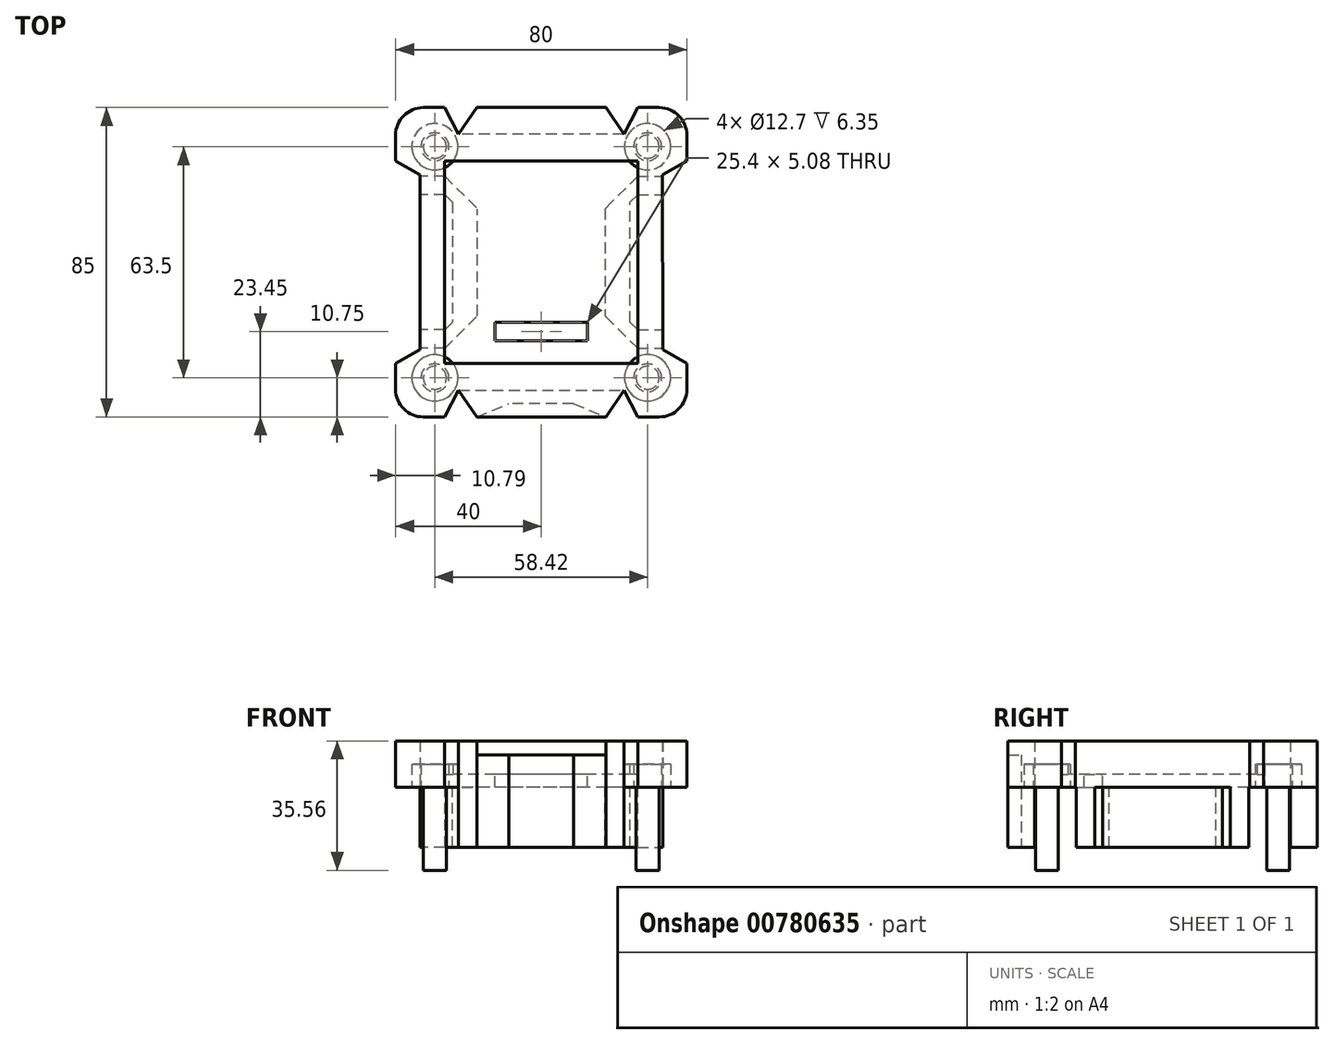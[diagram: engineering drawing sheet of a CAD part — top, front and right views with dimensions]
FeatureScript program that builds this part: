
annotation { "Feature Type Name" : "Feature", "Feature Type Description" : "" }
export const myFeature = defineFeature(function(context is Context, id is Id, definition is map)
    precondition{}
    {
        {
            var Q0;
            Q0=qCreatedBy(makeId("Top.planeOp"),FACE);
            var sketch = newSketch(context, id + "F0", { "sketchPlane" : qUnion([Q0])});
            skLineSegment(sketch, "E0.bottom", {"start": v(40, -42.5) * mm, "end": v(-40, -42.5) * mm});
            skLineSegment(sketch, "E0.top", {"start": v(40, 42.5) * mm, "end": v(-40, 42.5) * mm});
            skLineSegment(sketch, "E0.left", {"start": v(40, -42.5) * mm, "end": v(40, 42.5) * mm});
            skLineSegment(sketch, "E0.right", {"start": v(-40, -42.5) * mm, "end": v(-40, 42.5) * mm});
            skPoint(sketch, "E0.middle", {"position": v(0, 0) * mm});
            skSolve(sketch);
        }
        {
            var Q0;
            Q0=makeQuery(id+"F0.imprint","IMPRINT",FACE,{"disambiguationData":[TD([[makeQuery(id+"F0.imprint","IMPRINT",EDGE,{"derivedFrom":sQuery(id+"F0.wireOp",EDGE,"E0.bottom")}),-1.0]])]});
            extrude(context, id + "F1", {"entities" : qUnion([Q0]), "depth" : 25.4 * mm, "offsetDistance" : 25.4 * mm});
        }
        {
            var Q0;
            Q0=qCreatedBy(makeId("Front.planeOp"),FACE);
            var sketch = newSketch(context, id + "F2", { "sketchPlane" : qUnion([Q0])});
            skLineSegment(sketch, "E1.bottom", {"start": v(26.5, 3.57) * mm, "end": v(-26.5, 3.56) * mm});
            skLineSegment(sketch, "E1.top", {"start": v(26.5, 20.57) * mm, "end": v(-26.5, 20.56) * mm});
            skLineSegment(sketch, "E1.left", {"start": v(26.5, 3.57) * mm, "end": v(26.5, 20.57) * mm});
            skLineSegment(sketch, "E1.right", {"start": v(-26.5, 3.56) * mm, "end": v(-26.5, 20.57) * mm});
            skPoint(sketch, "E1.middle", {"position": v(0, 12.07) * mm});
            skSolve(sketch);
        }
        {
            var Q0;
            Q0=qSketchRegion(id+"F2",true);
            extrude(context, id + "F3", {"entities" : qUnion([Q0]), "operationType" : NewBodyOperationType.REMOVE, "oppositeDirection" : true, "depth" : 55.55 * mm, "offsetDistance" : 25.4 * mm, "symmetric" : true});
        }
        {
            var Q0;
            Q0=makeQuery(id+"F1.opExtrude","CAP_FACE",FACE,{"disambiguationData":[OSD([sQuery(id+"F0.wireOp",EDGE,"E0.bottom"),sQuery(id+"F0.wireOp",EDGE,"E0.top"),sQuery(id+"F0.wireOp",EDGE,"E0.left"),sQuery(id+"F0.wireOp",EDGE,"E0.right")])],"isStart":false});
            var sketch = newSketch(context, id + "F4", { "sketchPlane" : qUnion([Q0])});
            skLineSegment(sketch, "E2.bottom", {"start": v(40, -42.5) * mm, "end": v(-40, -42.5) * mm});
            skLineSegment(sketch, "E2.top", {"start": v(40, 42.5) * mm, "end": v(-40, 42.5) * mm});
            skLineSegment(sketch, "E2.left", {"start": v(40, -42.5) * mm, "end": v(40, 42.5) * mm});
            skLineSegment(sketch, "E2.right", {"start": v(-40, -42.5) * mm, "end": v(-40, 42.5) * mm});
            skPoint(sketch, "E2.middle", {"position": v(0, 0) * mm});
            skSolve(sketch);
        }
        {
            var Q0;
            Q0=qSketchRegion(id+"F4",true);
            extrude(context, id + "F5", {"entities" : qUnion([Q0]), "operationType" : NewBodyOperationType.REMOVE, "oppositeDirection" : true, "depth" : 12.7 * mm, "offsetDistance" : 25.4 * mm});
        }
        {
            var Q0;
            Q0=makeQuery(id+"F1.opExtrude","CAP_FACE",FACE,{"disambiguationData":[OSD([sQuery(id+"F0.wireOp",EDGE,"E0.bottom"),sQuery(id+"F0.wireOp",EDGE,"E0.top"),sQuery(id+"F0.wireOp",EDGE,"E0.left"),sQuery(id+"F0.wireOp",EDGE,"E0.right")])],"isStart":true});
            var sketch = newSketch(context, id + "F6", { "sketchPlane" : qUnion([Q0])});
            skCircle(sketch, "E3", {"center": v(-29.21, 31.75) * mm, "radius": 3.16 * mm});
            skCircle(sketch, "E4", {"center": v(29.21, 31.75) * mm, "radius": 3.16 * mm});
            skCircle(sketch, "E5", {"center": v(29.21, -31.75) * mm, "radius": 3.16 * mm});
            skCircle(sketch, "E6", {"center": v(-29.21, -31.75) * mm, "radius": 3.16 * mm});
            skSolve(sketch);
        }
        {
            var Q0;
            Q0 = qSketchRegion(id + "F6", true);
            extrude(context, id + "F7", {"entities" : qUnion([Q0]), "operationType" : NewBodyOperationType.ADD, "depth" : 22.86 * mm, "offsetDistance" : 25.4 * mm});
        }
        {
            var Q0;
            Q0=makeQuery(id+"F3.boolean.opBoolean","COPY",FACE,{"derivedFrom":makeQuery(id+"F3.opExtrude","SWEPT_FACE",FACE,{"disambiguationData":[OSD([sQuery(id+"F2.wireOp",EDGE,"E1.bottom")])]})});
            var sketch = newSketch(context, id + "F8", { "sketchPlane" : qUnion([Q0])});
            skLineSegment(sketch, "E7.bottom", {"start": v(12.7, -21.59) * mm, "end": v(-12.7, -21.59) * mm});
            skLineSegment(sketch, "E7.top", {"start": v(12.7, -16.51) * mm, "end": v(-12.7, -16.51) * mm});
            skLineSegment(sketch, "E7.left", {"start": v(12.7, -21.59) * mm, "end": v(12.7, -16.51) * mm});
            skLineSegment(sketch, "E7.right", {"start": v(-12.7, -21.59) * mm, "end": v(-12.7, -16.51) * mm});
            skPoint(sketch, "E7.middle", {"position": v(0, -19.05) * mm});
            skSolve(sketch);
        }
        {
            var Q0;
            Q0 = qSketchRegion(id + "F8", true);
            extrude(context, id + "F9", {"entities" : qUnion([Q0]), "operationType" : NewBodyOperationType.REMOVE, "oppositeDirection" : true, "depth" : 25.4 * mm, "offsetDistance" : 25.4 * mm});
        }
        {
            var Q0;
            Q0=makeQuery(id+"F1.opExtrude","SWEPT_EDGE",EDGE,{"disambiguationData":[OSD([sQuery(id+"F0.wireOp",EDGE,"E0.bottom"),sQuery(id+"F0.wireOp",EDGE,"E0.right")])]});
            fillet(context, id + "F10", {"entities" : qUnion([Q0]), "radius" : 7.62 * mm, "tangentPropagation" : true, "allowEdgeOverflow" : false});
        }
        {
            var Q0;
            Q0=makeQuery(id+"F1.opExtrude","SWEPT_EDGE",EDGE,{"disambiguationData":[OSD([sQuery(id+"F0.wireOp",EDGE,"E0.top"),sQuery(id+"F0.wireOp",EDGE,"E0.right")])]});
            fillet(context, id + "F11", {"entities" : qUnion([Q0]), "radius" : 7.62 * mm, "tangentPropagation" : true, "allowEdgeOverflow" : false});
        }
        {
            var Q0;
            Q0=makeQuery(id+"F1.opExtrude","SWEPT_EDGE",EDGE,{"disambiguationData":[OSD([sQuery(id+"F0.wireOp",EDGE,"E0.top"),sQuery(id+"F0.wireOp",EDGE,"E0.left")])]});
            fillet(context, id + "F12", {"entities" : qUnion([Q0]), "radius" : 7.62 * mm, "tangentPropagation" : true, "allowEdgeOverflow" : false});
        }
        {
            var Q0;
            Q0=makeQuery(id+"F1.opExtrude","SWEPT_EDGE",EDGE,{"disambiguationData":[OSD([sQuery(id+"F0.wireOp",EDGE,"E0.bottom"),sQuery(id+"F0.wireOp",EDGE,"E0.left")])]});
            fillet(context, id + "F13", {"entities" : qUnion([Q0]), "radius" : 7.62 * mm, "tangentPropagation" : true, "allowEdgeOverflow" : false});
        }
        {
            var Q0;
            Q0=makeQuery(id+"F1.opExtrude","CAP_FACE",FACE,{"disambiguationData":[OSD([sQuery(id+"F0.wireOp",EDGE,"E0.bottom"),sQuery(id+"F0.wireOp",EDGE,"E0.top"),sQuery(id+"F0.wireOp",EDGE,"E0.left"),sQuery(id+"F0.wireOp",EDGE,"E0.right")])],"isStart":true});
            var sketch = newSketch(context, id + "F14", { "sketchPlane" : qUnion([Q0])});
            skLineSegment(sketch, "E8", {"start": v(-26.48, 23.65) * mm, "end": v(-19.3, 16.47) * mm});
            skLineSegment(sketch, "E9", {"start": v(-26.48, -23.65) * mm, "end": v(-19.3, -16.47) * mm});
            skLineSegment(sketch, "E10", {"start": v(-24.38, -8.23) * mm, "end": v(-24.38, -16.47) * mm});
            skLineSegment(sketch, "E11", {"start": v(-24.38, -16.47) * mm, "end": v(-26.48, -18.57) * mm});
            skLineSegment(sketch, "E12", {"start": v(-24.38, -8.23) * mm, "end": v(-24.38, 0) * mm});
            skLineSegment(sketch, "E13", {"start": v(-24.38, 8.23) * mm, "end": v(-24.38, 0) * mm});
            skLineSegment(sketch, "E14", {"start": v(-24.38, 8.23) * mm, "end": v(-24.38, 16.47) * mm});
            skLineSegment(sketch, "E15", {"start": v(-24.38, 16.47) * mm, "end": v(-26.48, 18.57) * mm});
            skLineSegment(sketch, "E16", {"start": v(-26.48, 18.57) * mm, "end": v(-34.1, 18.57) * mm});
            skLineSegment(sketch, "E17", {"start": v(-26.48, 23.65) * mm, "end": v(-34.1, 23.65) * mm});
            skLineSegment(sketch, "E18", {"start": v(-34.1, 23.65) * mm, "end": v(-34.1, 18.57) * mm});
            skLineSegment(sketch, "E19", {"start": v(-26.48, -18.57) * mm, "end": v(-34.1, -18.57) * mm});
            skLineSegment(sketch, "E20", {"start": v(-26.48, -23.65) * mm, "end": v(-34.1, -23.65) * mm});
            skLineSegment(sketch, "E21", {"start": v(-34.1, -23.65) * mm, "end": v(-34.1, -18.57) * mm});
            skLineSegment(sketch, "E22", {"start": v(26.48, -23.65) * mm, "end": v(19.3, -16.47) * mm});
            skLineSegment(sketch, "E23", {"start": v(26.48, 23.65) * mm, "end": v(19.3, 16.47) * mm});
            skLineSegment(sketch, "E24", {"start": v(24.38, 8.23) * mm, "end": v(24.38, 16.47) * mm});
            skLineSegment(sketch, "E25", {"start": v(24.38, 16.47) * mm, "end": v(26.48, 18.57) * mm});
            skLineSegment(sketch, "E26", {"start": v(24.38, 8.23) * mm, "end": v(24.38, 0) * mm});
            skLineSegment(sketch, "E27", {"start": v(24.38, -8.23) * mm, "end": v(24.38, 0) * mm});
            skLineSegment(sketch, "E28", {"start": v(24.38, -8.23) * mm, "end": v(24.38, -16.47) * mm});
            skLineSegment(sketch, "E29", {"start": v(24.38, -16.47) * mm, "end": v(26.48, -18.57) * mm});
            skLineSegment(sketch, "E30", {"start": v(26.48, -18.57) * mm, "end": v(34.1, -18.57) * mm});
            skLineSegment(sketch, "E31", {"start": v(26.48, -23.65) * mm, "end": v(34.1, -23.65) * mm});
            skLineSegment(sketch, "E32", {"start": v(34.1, -23.65) * mm, "end": v(34.1, -18.57) * mm});
            skLineSegment(sketch, "E33", {"start": v(26.48, 18.57) * mm, "end": v(34.1, 18.57) * mm});
            skLineSegment(sketch, "E34", {"start": v(34.1, 18.57) * mm, "end": v(34.1, 23.65) * mm});
            skLineSegment(sketch, "E35", {"start": v(26.48, 23.65) * mm, "end": v(34.1, 23.65) * mm});
            skLineSegment(sketch, "E36", {"start": v(-17.5, 14.67) * mm, "end": v(-17.5, 0) * mm});
            skLineSegment(sketch, "E37", {"start": v(-19.3, 16.47) * mm, "end": v(-17.5, 14.67) * mm});
            skLineSegment(sketch, "E38", {"start": v(-17.5, 0) * mm, "end": v(-17.5, -14.67) * mm});
            skLineSegment(sketch, "E39", {"start": v(-19.3, -16.47) * mm, "end": v(-17.5, -14.67) * mm});
            skLineSegment(sketch, "E40", {"start": v(17.5, 0) * mm, "end": v(17.5, 14.67) * mm});
            skLineSegment(sketch, "E41", {"start": v(17.5, 14.67) * mm, "end": v(19.3, 16.47) * mm});
            skLineSegment(sketch, "E42", {"start": v(17.5, 0) * mm, "end": v(17.5, -14.67) * mm});
            skLineSegment(sketch, "E43", {"start": v(19.3, -16.47) * mm, "end": v(17.5, -14.67) * mm});
            skSolve(sketch);
        }
        {
            var Q0;
            Q0 = qSketchRegion(id + "F14", true);
            extrude(context, id + "F15", {"entities" : qUnion([Q0]), "operationType" : NewBodyOperationType.ADD, "depth" : 16.5 * mm, "offsetDistance" : 25.4 * mm});
        }
        {
            var Q0;
            Q0=makeQuery(id+"F1.opExtrude","CAP_FACE",FACE,{"disambiguationData":[OSD([sQuery(id+"F0.wireOp",EDGE,"E0.bottom"),sQuery(id+"F0.wireOp",EDGE,"E0.top"),sQuery(id+"F0.wireOp",EDGE,"E0.left"),sQuery(id+"F0.wireOp",EDGE,"E0.right")])],"isStart":true});
            var sketch = newSketch(context, id + "F16", { "sketchPlane" : qUnion([Q0])});
            skLineSegment(sketch, "E44.bottom", {"start": v(-17.5, -25.4) * mm, "end": v(17.5, -25.4) * mm});
            skLineSegment(sketch, "E44.top", {"start": v(-17.5, 25.4) * mm, "end": v(17.5, 25.4) * mm});
            skLineSegment(sketch, "E44.left", {"start": v(-17.5, -25.4) * mm, "end": v(-17.5, 25.4) * mm});
            skLineSegment(sketch, "E44.right", {"start": v(17.5, -25.4) * mm, "end": v(17.5, 25.4) * mm});
            skPoint(sketch, "E44.middle", {"position": v(0, 0) * mm});
            skSolve(sketch);
        }
        {
            var Q0;
            Q0 = qSketchRegion(id + "F16", true);
            extrude(context, id + "F17", {"entities" : qUnion([Q0]), "operationType" : NewBodyOperationType.REMOVE, "depth" : 25.4 * mm, "offsetDistance" : 25.4 * mm});
        }
        {
            var Q0;
            Q0=makeQuery(id+"F3.boolean.opBoolean","COPY",FACE,{"derivedFrom":makeQuery(id+"F3.opExtrude","SWEPT_FACE",FACE,{"disambiguationData":[OSD([sQuery(id+"F2.wireOp",EDGE,"E1.bottom")])]})});
            var sketch = newSketch(context, id + "F18", { "sketchPlane" : qUnion([Q0])});
            skLineSegment(sketch, "E45", {"start": v(26.5, -42.5) * mm, "end": v(22.69, -35.14) * mm});
            skLineSegment(sketch, "E46", {"start": v(-22.69, -35.14) * mm, "end": v(-26.5, -42.5) * mm});
            skLineSegment(sketch, "E47", {"start": v(40, -27.77) * mm, "end": v(33.33, -24) * mm});
            skLineSegment(sketch, "E48", {"start": v(33.25, 23.96) * mm, "end": v(33.33, -24) * mm});
            skLineSegment(sketch, "E49", {"start": v(40, 27.77) * mm, "end": v(33.25, 23.96) * mm});
            skLineSegment(sketch, "E50", {"start": v(-22.69, 35.14) * mm, "end": v(22.69, 35.14) * mm});
            skLineSegment(sketch, "E51", {"start": v(26.5, 42.5) * mm, "end": v(22.69, 35.14) * mm});
            skLineSegment(sketch, "E52", {"start": v(-26.5, 42.5) * mm, "end": v(-22.69, 35.14) * mm});
            skLineSegment(sketch, "E53", {"start": v(-33.25, 23.96) * mm, "end": v(-33.25, -23.96) * mm});
            skLineSegment(sketch, "E54", {"start": v(-40, 27.77) * mm, "end": v(-33.25, 23.96) * mm});
            skLineSegment(sketch, "E55", {"start": v(-40, -27.77) * mm, "end": v(-33.25, -23.96) * mm});
            skLineSegment(sketch, "E56", {"start": v(40, -27.77) * mm, "end": v(40, 27.77) * mm});
            skLineSegment(sketch, "E57", {"start": v(26.5, 42.5) * mm, "end": v(-26.5, 42.5) * mm});
            skLineSegment(sketch, "E58", {"start": v(-40, 27.77) * mm, "end": v(-40, -27.77) * mm});
            skLineSegment(sketch, "E59", {"start": v(-26.5, -42.5) * mm, "end": v(26.5, -42.5) * mm});
            skLineSegment(sketch, "E60", {"start": v(22.69, -35.14) * mm, "end": v(-22.69, -35.14) * mm});
            skLineSegment(sketch, "E61", {"start": v(40, 27.77) * mm, "end": v(40, -27.77) * mm});
            skSolve(sketch);
        }
        {
            var Q0;
            Q0 = qSketchRegion(id + "F18", true);
            extrude(context, id + "F19", {"entities" : qUnion([Q0]), "operationType" : NewBodyOperationType.REMOVE, "depth" : 76.2 * mm, "offsetDistance" : 25.4 * mm, "symmetric" : true});
        }
        {
            var Q0;
            Q0=makeQuery(id+"F17.boolean.opBoolean","MERGE",FACE,{"derivedFrom":[makeQuery(id+"F1.opExtrude","CAP_FACE",FACE,{"disambiguationData":[OSD([sQuery(id+"F0.wireOp",EDGE,"E0.bottom"),sQuery(id+"F0.wireOp",EDGE,"E0.top"),sQuery(id+"F0.wireOp",EDGE,"E0.left"),sQuery(id+"F0.wireOp",EDGE,"E0.right")])],"isStart":true}),makeQuery(id+"F17.opExtrude","CAP_FACE",FACE,{"disambiguationData":[OSD([sQuery(id+"F16.wireOp",EDGE,"E44.bottom"),sQuery(id+"F16.wireOp",EDGE,"E44.top"),sQuery(id+"F16.wireOp",EDGE,"E44.left"),sQuery(id+"F16.wireOp",EDGE,"E44.right")])],"isStart":true})]});
            var sketch = newSketch(context, id + "F20", { "sketchPlane" : qUnion([Q0])});
            skCircle(sketch, "E62", {"center": v(-29.21, 31.75) * mm, "radius": 6.35 * mm});
            skCircle(sketch, "E63", {"center": v(-29.21, 31.75) * mm, "radius": 3.81 * mm});
            skCircle(sketch, "E64", {"center": v(29.21, 31.75) * mm, "radius": 3.81 * mm});
            skCircle(sketch, "E65", {"center": v(29.21, 31.75) * mm, "radius": 6.35 * mm});
            skCircle(sketch, "E66", {"center": v(29.21, -31.75) * mm, "radius": 3.81 * mm});
            skCircle(sketch, "E67", {"center": v(29.21, -31.75) * mm, "radius": 6.35 * mm});
            skCircle(sketch, "E68", {"center": v(-29.21, -31.75) * mm, "radius": 3.81 * mm});
            skCircle(sketch, "E69", {"center": v(-29.21, -31.75) * mm, "radius": 6.35 * mm});
            skSolve(sketch);
        }
        {
            var Q0;
            Q0 = qSketchRegion(id + "F20", true);
            extrude(context, id + "F21", {"entities" : qUnion([Q0]), "operationType" : NewBodyOperationType.REMOVE, "oppositeDirection" : true, "depth" : 6.35 * mm, "offsetDistance" : 25.4 * mm});
        }
        {
            var Q0;
            Q0=makeQuery(id+"F5.boolean.opBoolean","COPY",FACE,{"derivedFrom":makeQuery(id+"F5.opExtrude","CAP_FACE",FACE,{"disambiguationData":[OSD([sQuery(id+"F4.wireOp",EDGE,"E2.bottom"),sQuery(id+"F4.wireOp",EDGE,"E2.top"),sQuery(id+"F4.wireOp",EDGE,"E2.left"),sQuery(id+"F4.wireOp",EDGE,"E2.right")])],"isStart":false})});
            var sketch = newSketch(context, id + "F22", { "sketchPlane" : qUnion([Q0])});
            skLineSegment(sketch, "E70", {"start": v(-22.7, -35.14) * mm, "end": v(-17.7, -42.5) * mm});
            skLineSegment(sketch, "E71", {"start": v(22.69, -35.14) * mm, "end": v(17.7, -42.5) * mm});
            skLineSegment(sketch, "E72", {"start": v(-22.7, -35.14) * mm, "end": v(22.69, -35.14) * mm});
            skLineSegment(sketch, "E73", {"start": v(17.7, -42.5) * mm, "end": v(-17.7, -42.5) * mm});
            skLineSegment(sketch, "E74", {"start": v(-22.7, 35.14) * mm, "end": v(-17.7, 42.5) * mm});
            skLineSegment(sketch, "E75", {"start": v(-17.7, 42.5) * mm, "end": v(17.7, 42.5) * mm});
            skLineSegment(sketch, "E76", {"start": v(17.7, 42.5) * mm, "end": v(22.69, 35.14) * mm});
            skLineSegment(sketch, "E77", {"start": v(22.69, 35.14) * mm, "end": v(-22.7, 35.14) * mm});
            skSolve(sketch);
        }
        {
            var Q0;
            Q0 = qSketchRegion(id + "F22", true);
            extrude(context, id + "F23", {"entities" : qUnion([Q0]), "operationType" : NewBodyOperationType.ADD, "oppositeDirection" : true, "depth" : 29.2 * mm, "offsetDistance" : 25.4 * mm});
        }
        {
            var Q0;
            Q0=makeQuery(id+"F23.opExtrude","CAP_FACE",FACE,{"disambiguationData":[OSD([sQuery(id+"F22.wireOp",EDGE,"E70"),sQuery(id+"F22.wireOp",EDGE,"E71"),sQuery(id+"F22.wireOp",EDGE,"E72"),sQuery(id+"F22.wireOp",EDGE,"E73")])],"isStart":false});
            var sketch = newSketch(context, id + "F24", { "sketchPlane" : qUnion([Q0])});
            skLineSegment(sketch, "E78", {"start": v(0, 38.82) * mm, "end": v(0, 35.14) * mm});
            skLineSegment(sketch, "E79", {"start": v(-17.7, 42.5) * mm, "end": v(-8.85, 38.82) * mm});
            skLineSegment(sketch, "E80", {"start": v(0, 38.82) * mm, "end": v(-8.85, 38.82) * mm});
            skLineSegment(sketch, "E81", {"start": v(0, 38.82) * mm, "end": v(8.85, 38.82) * mm});
            skLineSegment(sketch, "E82", {"start": v(8.85, 38.82) * mm, "end": v(17.7, 42.5) * mm});
            skLineSegment(sketch, "E83", {"start": v(17.7, 42.5) * mm, "end": v(-17.7, 42.5) * mm});
            skSolve(sketch);
        }
        {
            var Q0;
            Q0 = qSketchRegion(id + "F24", true);
            extrude(context, id + "F25", {"entities" : qUnion([Q0]), "operationType" : NewBodyOperationType.REMOVE, "oppositeDirection" : true, "depth" : 25.4 * mm, "offsetDistance" : 25.4 * mm});
        }
    });
